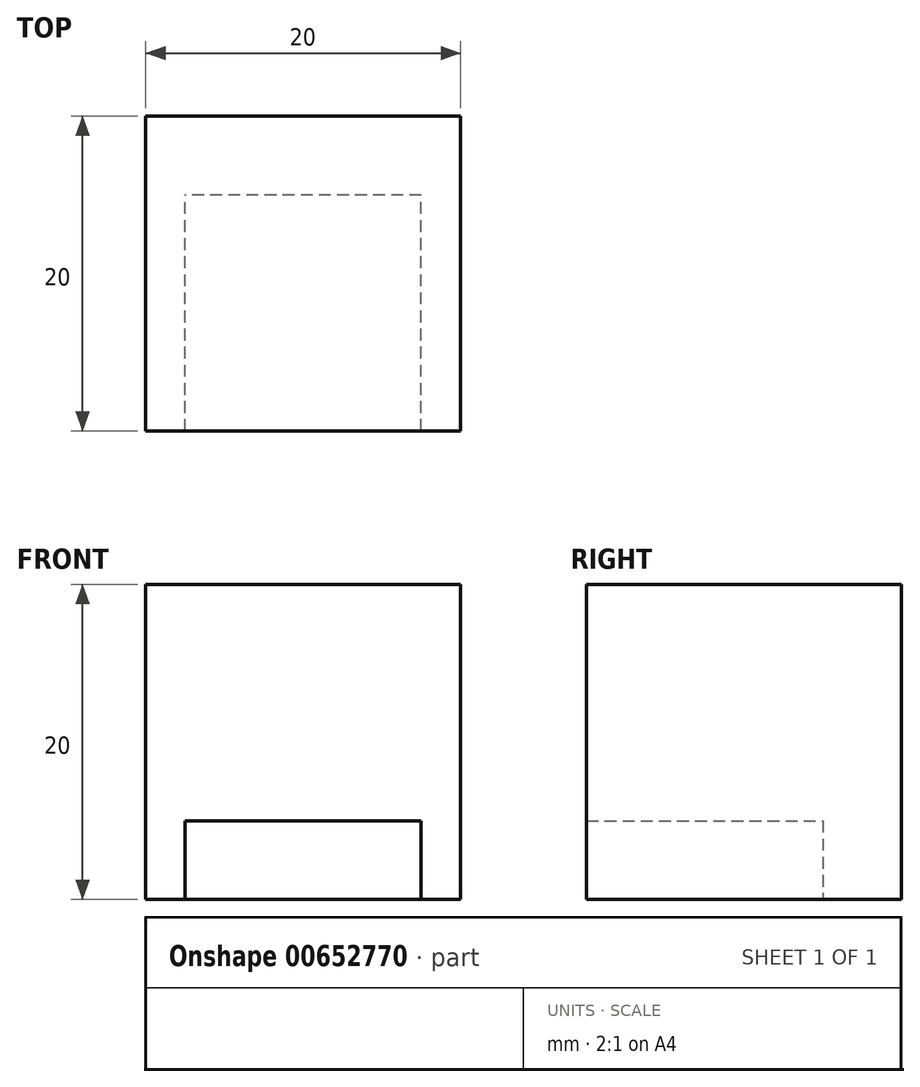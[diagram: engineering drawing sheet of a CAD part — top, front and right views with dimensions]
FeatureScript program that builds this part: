
annotation { "Feature Type Name" : "Feature", "Feature Type Description" : "" }
export const myFeature = defineFeature(function(context is Context, id is Id, definition is map)
    precondition{}
    {
        {
            var Q0;
            Q0=qCreatedBy(makeId("Top.planeOp"),FACE);
            var sketch = newSketch(context, id + "F0", { "sketchPlane" : qUnion([Q0])});
            skLineSegment(sketch, "E0.bottom", {"start": v(0, 0) * mm, "end": v(-20, 0) * mm});
            skLineSegment(sketch, "E0.top", {"start": v(0, 20) * mm, "end": v(-20, 20) * mm});
            skLineSegment(sketch, "E0.left", {"start": v(0, 0) * mm, "end": v(0, 20) * mm});
            skLineSegment(sketch, "E0.right", {"start": v(-20, 0) * mm, "end": v(-20, 20) * mm});
            skSolve(sketch);
        }
        {
            var Q0;
            Q0=makeQuery(id+"F0.imprint","IMPRINT",FACE,{"disambiguationData":[TD([[makeQuery(id+"F0.imprint","IMPRINT",EDGE,{"derivedFrom":sQuery(id+"F0.wireOp",EDGE,"E0.bottom")}),-1.0]])]});
            extrude(context, id + "F1", {"entities" : qUnion([Q0]), "depth" : 20 * mm, "offsetDistance" : 25 * mm});
        }
        {
            var Q0;
            Q0=qCreatedBy(makeId("Top.planeOp"),FACE);
            var sketch = newSketch(context, id + "F2", { "sketchPlane" : qUnion([Q0])});
            skLineSegment(sketch, "E1", {"start": v(0, 0) * mm, "end": v(-2.5, 0) * mm});
            skLineSegment(sketch, "E2.bottom", {"start": v(-2.5, 0) * mm, "end": v(-17.5, 0) * mm});
            skLineSegment(sketch, "E2.top", {"start": v(-2.5, 15) * mm, "end": v(-17.5, 15) * mm});
            skLineSegment(sketch, "E2.left", {"start": v(-2.5, 0) * mm, "end": v(-2.5, 15) * mm});
            skLineSegment(sketch, "E2.right", {"start": v(-17.5, 0) * mm, "end": v(-17.5, 15) * mm});
            skSolve(sketch);
        }
        {
            var Q0;
            Q0=makeQuery(id+"F2.imprint","IMPRINT",FACE,{"disambiguationData":[TD([[makeQuery(id+"F2.imprint","IMPRINT",EDGE,{"derivedFrom":sQuery(id+"F2.wireOp",EDGE,"E2.bottom")}),-1.0]])]});
            var Q1;
            Q1=sQuery(id+"F2.wireOp",EDGE,"E2.top");
            var Q2;
            Q2=sQuery(id+"F2.wireOp",EDGE,"E2.left");
            var Q3;
            Q3=sQuery(id+"F2.wireOp",EDGE,"E2.right");
            var Q4;
            Q4=sQuery(id+"F2.wireOp",EDGE,"E2.bottom");
            extrude(context, id + "F3", {"entities" : qUnion([Q0]), "operationType" : NewBodyOperationType.REMOVE, "surfaceEntities" : qUnion([Q1, Q2, Q3, Q4]), "depth" : 5 * mm, "offsetDistance" : 25 * mm});
        }
    });
